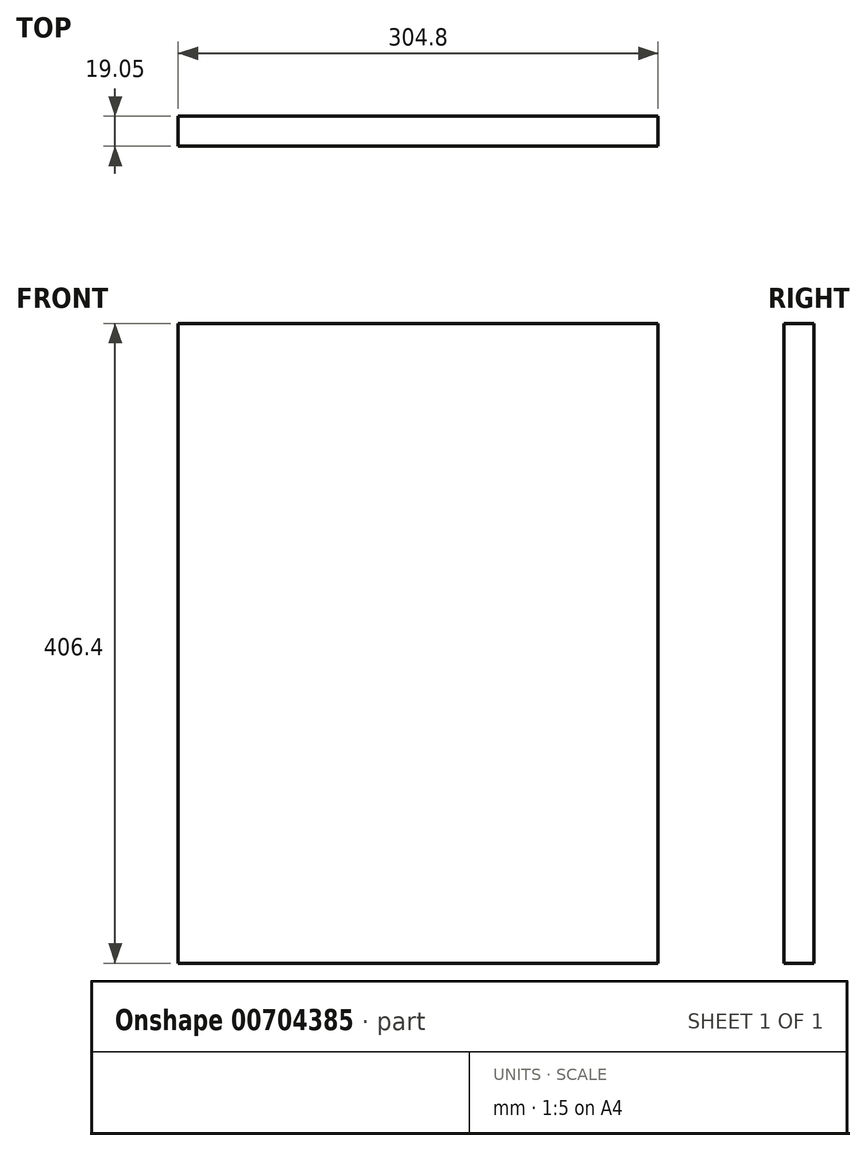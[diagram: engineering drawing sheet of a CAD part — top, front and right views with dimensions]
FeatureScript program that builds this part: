
annotation { "Feature Type Name" : "Feature", "Feature Type Description" : "" }
export const myFeature = defineFeature(function(context is Context, id is Id, definition is map)
    precondition{}
    {
        {
            var Q0;
            Q0=qCreatedBy(makeId("Front.planeOp"),FACE);
            var sketch = newSketch(context, id + "F0", { "sketchPlane" : qUnion([Q0])});
            skLineSegment(sketch, "E0.bottom", {"start": v(152.4, -203.2) * mm, "end": v(-152.4, -203.2) * mm});
            skLineSegment(sketch, "E0.top", {"start": v(152.4, 203.2) * mm, "end": v(-152.4, 203.2) * mm});
            skLineSegment(sketch, "E0.left", {"start": v(152.4, -203.2) * mm, "end": v(152.4, 203.2) * mm});
            skLineSegment(sketch, "E0.right", {"start": v(-152.4, -203.2) * mm, "end": v(-152.4, 203.2) * mm});
            skPoint(sketch, "E0.middle", {"position": v(0, 0) * mm});
            skSolve(sketch);
        }
        {
            var Q0;
            Q0=qSketchRegion(id+"F0",true);
            extrude(context, id + "F1", {"entities" : qUnion([Q0]), "depth" : 19.05 * mm, "offsetDistance" : 25.4 * mm});
        }
    });
